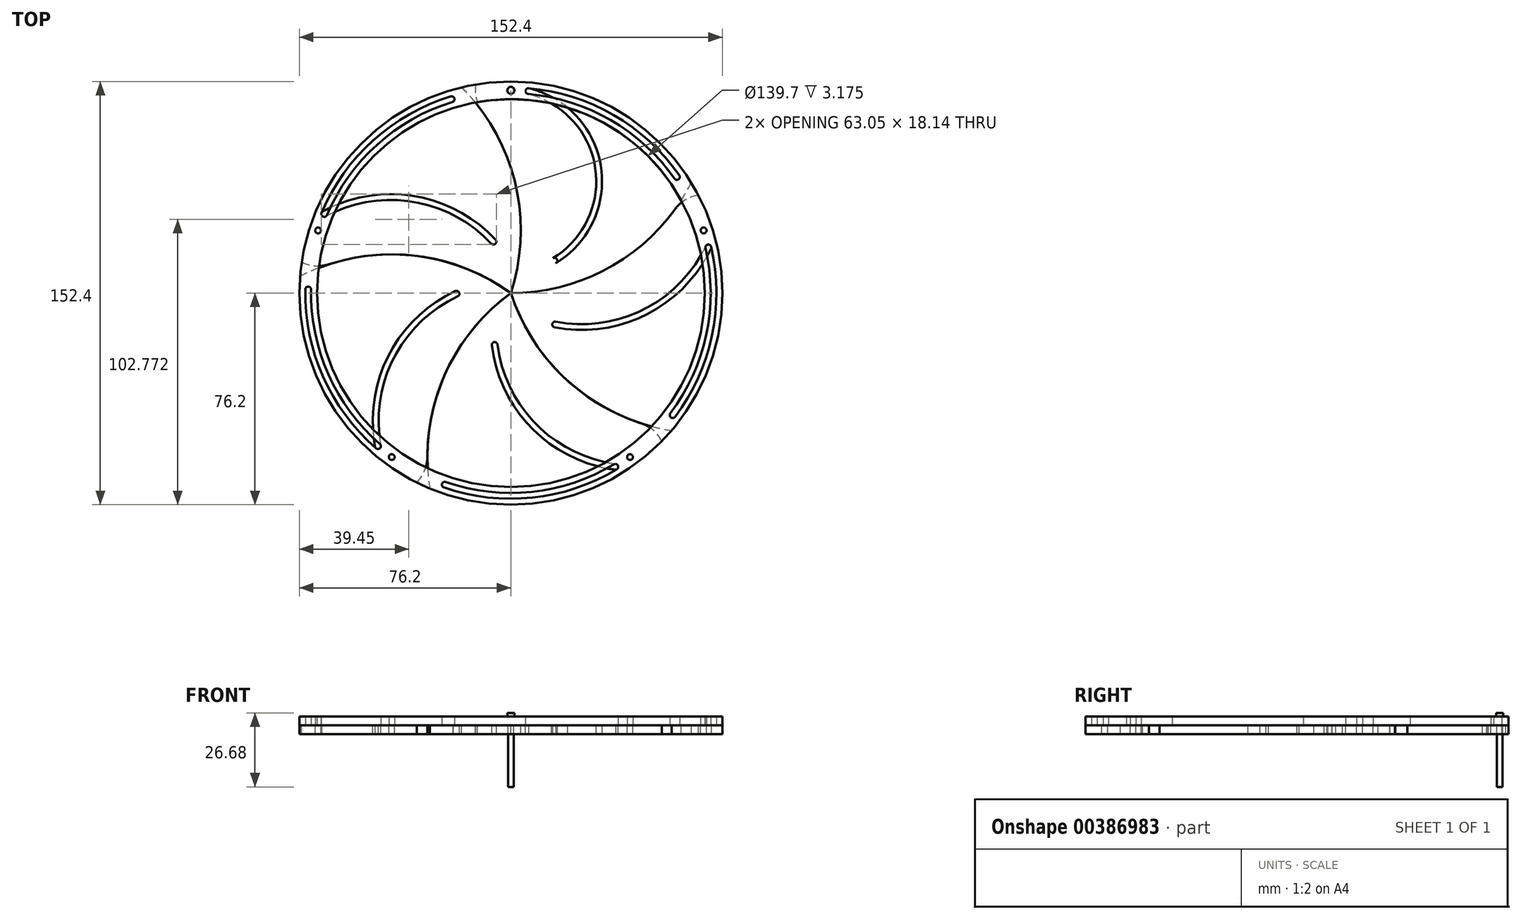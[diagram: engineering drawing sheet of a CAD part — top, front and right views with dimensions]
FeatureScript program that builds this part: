
annotation { "Feature Type Name" : "Feature", "Feature Type Description" : "" }
export const myFeature = defineFeature(function(context is Context, id is Id, definition is map)
    precondition{}
    {
        {
            var Q0;
            Q0=qCreatedBy(makeId("Top.planeOp"),FACE);
            var sketch = newSketch(context, id + "F0", { "sketchPlane" : qUnion([Q0])});
            skCircle(sketch, "E0", {"center": v(0, 0) * mm, "radius": 76.2 * mm});
            skCircle(sketch, "E1", {"center": v(0, 73.03) * mm, "radius": 1.05 * mm});
            skArc(sketch, "E2", {"start": v(0, 0) * mm, "mid": v(38.1, 10.73) * mm, "end": v(65, 39.76) * mm});
            skArc(sketch, "E3.1.0", {"start": v(0, 0) * mm, "mid": v(1.57, 39.55) * mm, "end": v(-17.72, 74.11) * mm});
            skCircle(sketch, "E3.1.1", {"center": v(-69.45, 22.57) * mm, "radius": 1.05 * mm});
            skArc(sketch, "E3.2.0", {"start": v(0, 0) * mm, "mid": v(-37.13, 13.72) * mm, "end": v(-75.96, 6.05) * mm});
            skCircle(sketch, "E3.2.1", {"center": v(-42.92, -59.08) * mm, "radius": 1.05 * mm});
            skArc(sketch, "E3.3.0", {"start": v(0, 0) * mm, "mid": v(-24.52, -31.07) * mm, "end": v(-29.22, -70.37) * mm});
            skCircle(sketch, "E3.3.1", {"center": v(42.92, -59.08) * mm, "radius": 1.05 * mm});
            skArc(sketch, "E3.4.0", {"start": v(0, 0) * mm, "mid": v(21.98, -32.92) * mm, "end": v(57.9, -49.54) * mm});
            skCircle(sketch, "E3.4.1", {"center": v(69.45, 22.57) * mm, "radius": 1.05 * mm});
            skArc(sketch, "E4", {"start": v(-12.64, 75.14) * mm, "mid": v(-12.48, 70.09) * mm, "end": v(-10.37, 65.49) * mm});
            skArc(sketch, "E5", {"start": v(6.44, 73.8) * mm, "mid": v(5.3, 72.84) * mm, "end": v(6.25, 71.7) * mm});
            skArc(sketch, "E6", {"start": v(58.97, 41.27) * mm, "mid": v(60.43, 41) * mm, "end": v(60.7, 42.47) * mm});
            skArc(sketch, "E7.trimOffspring", {"start": v(60.7, 42.47) * mm, "mid": v(37.04, 64.15) * mm, "end": v(6.44, 73.8) * mm});
            skArc(sketch, "E8.trimOffspring", {"start": v(58.97, 41.27) * mm, "mid": v(35.99, 62.33) * mm, "end": v(6.25, 71.7) * mm});
            skArc(sketch, "E9", {"start": v(14.79, 12.2) * mm, "mid": v(15.2, 10.78) * mm, "end": v(16.62, 11.2) * mm});
            skArc(sketch, "E10.1.0", {"start": v(-7.04, 17.84) * mm, "mid": v(-35.22, 32.9) * mm, "end": v(-66.73, 27.6) * mm});
            skArc(sketch, "E10.1.1", {"start": v(-5.5, 19.27) * mm, "mid": v(-35.07, 35) * mm, "end": v(-68.05, 29.26) * mm});
            skArc(sketch, "E10.1.2", {"start": v(-68.2, 28.92) * mm, "mid": v(-67.64, 27.55) * mm, "end": v(-66.26, 28.1) * mm});
            skArc(sketch, "E10.1.3", {"start": v(-21.64, 70.84) * mm, "mid": v(-49.57, 55.05) * mm, "end": v(-68.2, 28.92) * mm});
            skArc(sketch, "E10.1.4", {"start": v(-21.02, 68.84) * mm, "mid": v(-48.16, 53.49) * mm, "end": v(-66.26, 28.1) * mm});
            skArc(sketch, "E10.1.5", {"start": v(-21.02, 68.84) * mm, "mid": v(-20.33, 70.15) * mm, "end": v(-21.64, 70.84) * mm});
            skArc(sketch, "E10.1.6", {"start": v(-7.04, 17.84) * mm, "mid": v(-5.56, 17.78) * mm, "end": v(-5.5, 19.27) * mm});
            skArc(sketch, "E10.1.7", {"start": v(-75.37, 11.2) * mm, "mid": v(-70.51, 9.79) * mm, "end": v(-65.49, 10.37) * mm});
            skArc(sketch, "E10.2.0", {"start": v(-19.14, -1.19) * mm, "mid": v(-42.17, -23.33) * mm, "end": v(-46.86, -54.94) * mm});
            skArc(sketch, "E10.2.1", {"start": v(-20.03, 0.72) * mm, "mid": v(-44.12, -22.53) * mm, "end": v(-48.86, -55.68) * mm});
            skArc(sketch, "E10.2.2", {"start": v(-48.58, -55.92) * mm, "mid": v(-47.1, -55.81) * mm, "end": v(-47.2, -54.33) * mm});
            skArc(sketch, "E10.2.3", {"start": v(-74.06, 1.31) * mm, "mid": v(-67.67, -30.13) * mm, "end": v(-48.58, -55.92) * mm});
            skArc(sketch, "E10.2.4", {"start": v(-71.96, 1.28) * mm, "mid": v(-65.75, -29.27) * mm, "end": v(-47.2, -54.33) * mm});
            skArc(sketch, "E10.2.5", {"start": v(-71.96, 1.28) * mm, "mid": v(-73, 2.34) * mm, "end": v(-74.06, 1.31) * mm});
            skArc(sketch, "E10.2.6", {"start": v(-19.14, -1.19) * mm, "mid": v(-18.63, 0.2) * mm, "end": v(-20.03, 0.72) * mm});
            skArc(sketch, "E10.2.7", {"start": v(-33.94, -68.22) * mm, "mid": v(-31.1, -64.04) * mm, "end": v(-30.1, -59.08) * mm});
            skArc(sketch, "E10.3.0", {"start": v(-4.79, -18.57) * mm, "mid": v(9.16, -47.31) * mm, "end": v(37.77, -61.54) * mm});
            skArc(sketch, "E10.3.1", {"start": v(-6.87, -18.83) * mm, "mid": v(7.8, -48.92) * mm, "end": v(37.85, -63.67) * mm});
            skArc(sketch, "E10.3.2", {"start": v(38.17, -63.48) * mm, "mid": v(38.53, -62.04) * mm, "end": v(37.09, -61.68) * mm});
            skArc(sketch, "E10.3.3", {"start": v(-24.14, -70.03) * mm, "mid": v(7.74, -73.67) * mm, "end": v(38.17, -63.48) * mm});
            skArc(sketch, "E10.3.4", {"start": v(-23.45, -68.05) * mm, "mid": v(7.52, -71.58) * mm, "end": v(37.09, -61.68) * mm});
            skArc(sketch, "E10.3.5", {"start": v(-23.45, -68.05) * mm, "mid": v(-24.79, -68.7) * mm, "end": v(-24.14, -70.03) * mm});
            skArc(sketch, "E10.3.6", {"start": v(-4.79, -18.57) * mm, "mid": v(-5.96, -17.66) * mm, "end": v(-6.87, -18.83) * mm});
            skArc(sketch, "E10.3.7", {"start": v(54.4, -53.36) * mm, "mid": v(51.3, -49.37) * mm, "end": v(46.88, -46.88) * mm});
            skArc(sketch, "E10.4.0", {"start": v(16.18, -10.29) * mm, "mid": v(47.83, -5.9) * mm, "end": v(70.2, 16.9) * mm});
            skArc(sketch, "E10.4.1", {"start": v(15.78, -12.35) * mm, "mid": v(48.94, -7.7) * mm, "end": v(72.25, 16.33) * mm});
            skArc(sketch, "E10.4.2", {"start": v(72.17, 16.68) * mm, "mid": v(70.91, 17.47) * mm, "end": v(70.13, 16.21) * mm});
            skArc(sketch, "E10.4.3", {"start": v(59.15, -44.6) * mm, "mid": v(72.46, -15.4) * mm, "end": v(72.17, 16.68) * mm});
            skArc(sketch, "E10.4.4", {"start": v(57.47, -43.33) * mm, "mid": v(70.4, -14.96) * mm, "end": v(70.13, 16.21) * mm});
            skArc(sketch, "E10.4.5", {"start": v(57.47, -43.33) * mm, "mid": v(57.68, -44.8) * mm, "end": v(59.15, -44.6) * mm});
            skArc(sketch, "E10.4.6", {"start": v(16.18, -10.29) * mm, "mid": v(14.95, -11.12) * mm, "end": v(15.78, -12.35) * mm});
            skArc(sketch, "E10.4.7", {"start": v(67.56, 35.25) * mm, "mid": v(62.8, 33.53) * mm, "end": v(59.08, 30.1) * mm});
            skCircle(sketch, "E11", {"center": v(0, 0) * mm, "radius": 69.85 * mm});
            skCircle(sketch, "E12", {"center": v(15.7, 11.7) * mm, "radius": 1.05 * mm});
            skArc(sketch, "E13", {"start": v(6.6, 73.77) * mm, "mid": v(5.3, 72.92) * mm, "end": v(6.25, 71.7) * mm});
            skArc(sketch, "E14", {"start": v(15.7, 11.7) * mm, "mid": v(16.15, 11.98) * mm, "end": v(16.6, 12.26) * mm});
            skArc(sketch, "E15", {"start": v(15.16, 12.6) * mm, "mid": v(30.38, 45.2) * mm, "end": v(6.1, 71.73) * mm});
            skArc(sketch, "E16", {"start": v(16.25, 10.8) * mm, "mid": v(32.45, 45.55) * mm, "end": v(6.52, 73.79) * mm});
            skArc(sketch, "E17.trimOffspring", {"start": v(-20.72, 68.99) * mm, "mid": v(-20.75, 68.97) * mm, "end": v(-20.78, 68.95) * mm});
            skSolve(sketch);
        }
        {
            var Q0;
            Q0=qSketchRegion(id+"F0",true);
            var Q1;
            {var subQ1=sQuery(id+"F0.wireOp",EDGE,"E10.1.2");var subQ7=sQuery(id+"F0.wireOp",EDGE,"E10.1.0");var subQ8=makeQuery(id+"F0.imprint","INTERSECT",VERTEX,{"derivedFrom":[subQ7,subQ1]});Q1=makeQuery(id+"F0.imprint","IMPRINT",FACE,{"disambiguationData":[TD([[makeQuery(id+"F0.imprint","IMPRINT",EDGE,{"disambiguationData":[TD([[subQ8,1.0]])],"derivedFrom":subQ7}),-1.0]])]});}
            var Q2;
            {var subQ1=sQuery(id+"F0.wireOp",EDGE,"E5");var subQ6=sQuery(id+"F0.wireOp",EDGE,"E8.trimOffspring");var subQ9=makeQuery(id+"F0.imprint","INTERSECT",VERTEX,{"derivedFrom":[subQ1,subQ6]});Q2=makeQuery(id+"F0.imprint","IMPRINT",FACE,{"disambiguationData":[TD([[makeQuery(id+"F0.imprint","IMPRINT",EDGE,{"disambiguationData":[TD([[subQ9,1.0]])],"derivedFrom":subQ1}),-1.0]])]});}
            var Q3;
            {var subQ1=sQuery(id+"F0.wireOp",EDGE,"E10.4.2");var subQ7=sQuery(id+"F0.wireOp",EDGE,"E10.4.0");var subQ8=makeQuery(id+"F0.imprint","INTERSECT",VERTEX,{"derivedFrom":[subQ7,subQ1]});Q3=makeQuery(id+"F0.imprint","IMPRINT",FACE,{"disambiguationData":[TD([[makeQuery(id+"F0.imprint","IMPRINT",EDGE,{"disambiguationData":[TD([[subQ8,1.0]])],"derivedFrom":subQ7}),-1.0]])]});}
            var Q4;
            {var subQ1=sQuery(id+"F0.wireOp",EDGE,"E10.3.2");var subQ7=sQuery(id+"F0.wireOp",EDGE,"E10.3.0");var subQ8=makeQuery(id+"F0.imprint","INTERSECT",VERTEX,{"derivedFrom":[subQ7,subQ1]});Q4=makeQuery(id+"F0.imprint","IMPRINT",FACE,{"disambiguationData":[TD([[makeQuery(id+"F0.imprint","IMPRINT",EDGE,{"disambiguationData":[TD([[subQ8,1.0]])],"derivedFrom":subQ7}),-1.0]])]});}
            var Q5;
            {var subQ1=sQuery(id+"F0.wireOp",EDGE,"E10.2.2");var subQ7=sQuery(id+"F0.wireOp",EDGE,"E10.2.0");var subQ8=makeQuery(id+"F0.imprint","INTERSECT",VERTEX,{"derivedFrom":[subQ7,subQ1]});Q5=makeQuery(id+"F0.imprint","IMPRINT",FACE,{"disambiguationData":[TD([[makeQuery(id+"F0.imprint","IMPRINT",EDGE,{"disambiguationData":[TD([[subQ8,1.0]])],"derivedFrom":subQ7}),-1.0]])]});}
            var Q6;
            {var subQ1=sQuery(id+"F0.wireOp",EDGE,"E13");var subQ7=sQuery(id+"F0.wireOp",EDGE,"E8.trimOffspring");var subQ8=makeQuery(id+"F0.imprint","INTERSECT",VERTEX,{"derivedFrom":[subQ7,subQ1]});Q6=makeQuery(id+"F0.imprint","IMPRINT",FACE,{"disambiguationData":[TD([[makeQuery(id+"F0.imprint","IMPRINT",EDGE,{"disambiguationData":[TD([[subQ8,1.0]])],"derivedFrom":subQ7}),1.0]])]});}
            extrude(context, id + "F1", {"entities" : qUnion([Q0, Q1, Q2, Q3, Q4, Q5, Q6]), "depth" : 3.17 * mm});
        }
        {
            var Q0;
            {var subQ10=sQuery(id+"F0.wireOp",EDGE,"E9");Q0=makeQuery(id+"F0.imprint","IMPRINT",FACE,{"disambiguationData":[TD([[makeQuery(id+"F0.imprint","IMPRINT",EDGE,{"derivedFrom":subQ10}),-1.0]])]});}
            var Q1;
            Q1=makeQuery(id+"F0.imprint","IMPRINT",FACE,{"disambiguationData":[TD([[makeQuery(id+"F0.imprint","IMPRINT",EDGE,{"derivedFrom":sQuery(id+"F0.wireOp",EDGE,"E1")}),-1.0]])]});
            var Q2;
            {var subQ0=sQuery(id+"F0.wireOp",EDGE,"E6");Q2=makeQuery(id+"F0.imprint","IMPRINT",FACE,{"disambiguationData":[TD([[makeQuery(id+"F0.imprint","IMPRINT",EDGE,{"derivedFrom":subQ0}),1.0]])]});}
            var Q3;
            {var subQ11=sQuery(id+"F0.wireOp",EDGE,"E12");var subQ13=makeQuery(id+"F0.imprint","IMPRINT",VERTEX,{"disambiguationData":[OD(1.0)],"derivedFrom":subQ11});Q3=makeQuery(id+"F0.imprint","IMPRINT",FACE,{"disambiguationData":[TD([[makeQuery(id+"F0.imprint","IMPRINT",EDGE,{"disambiguationData":[TD([[subQ13,1.0]])],"derivedFrom":subQ11}),-1.0]])]});}
            extrude(context, id + "F2", {"entities" : qUnion([Q0, Q1, Q2, Q3]), "depth" : -3.17 * mm});
        }
        {
            var Q0;
            {var subQ0=sQuery(id+"F0.wireOp",EDGE,"E10.4.6");Q0=makeQuery(id+"F0.imprint","IMPRINT",FACE,{"disambiguationData":[TD([[makeQuery(id+"F0.imprint","IMPRINT",EDGE,{"derivedFrom":subQ0}),-1.0]])]});}
            var Q1;
            Q1=makeQuery(id+"F0.imprint","IMPRINT",FACE,{"disambiguationData":[TD([[makeQuery(id+"F0.imprint","IMPRINT",EDGE,{"derivedFrom":sQuery(id+"F0.wireOp",EDGE,"E3.4.1")}),-1.0]])]});
            var Q2;
            {var subQ5=sQuery(id+"F0.wireOp",EDGE,"E10.4.5");Q2=makeQuery(id+"F0.imprint","IMPRINT",FACE,{"disambiguationData":[TD([[makeQuery(id+"F0.imprint","IMPRINT",EDGE,{"derivedFrom":subQ5}),1.0]])]});}
            extrude(context, id + "F3", {"entities" : qUnion([Q0, Q1, Q2]), "oppositeDirection" : true, "depth" : 3.17 * mm});
        }
        {
            var Q0;
            {var subQ5=sQuery(id+"F0.wireOp",EDGE,"E10.1.5");Q0=makeQuery(id+"F0.imprint","IMPRINT",FACE,{"disambiguationData":[TD([[makeQuery(id+"F0.imprint","IMPRINT",EDGE,{"derivedFrom":subQ5}),1.0]])]});}
            var Q1;
            Q1=makeQuery(id+"F0.imprint","IMPRINT",FACE,{"disambiguationData":[TD([[makeQuery(id+"F0.imprint","IMPRINT",EDGE,{"derivedFrom":sQuery(id+"F0.wireOp",EDGE,"E3.1.1")}),-1.0]])]});
            var Q2;
            {var subQ5=sQuery(id+"F0.wireOp",EDGE,"E10.1.6");Q2=makeQuery(id+"F0.imprint","IMPRINT",FACE,{"disambiguationData":[TD([[makeQuery(id+"F0.imprint","IMPRINT",EDGE,{"derivedFrom":subQ5}),-1.0]])]});}
            extrude(context, id + "F4", {"entities" : qUnion([Q0, Q1, Q2]), "oppositeDirection" : true, "depth" : 3.17 * mm});
        }
        {
            var Q0;
            {var subQ5=sQuery(id+"F0.wireOp",EDGE,"E10.2.5");Q0=makeQuery(id+"F0.imprint","IMPRINT",FACE,{"disambiguationData":[TD([[makeQuery(id+"F0.imprint","IMPRINT",EDGE,{"derivedFrom":subQ5}),1.0]])]});}
            var Q1;
            Q1=makeQuery(id+"F0.imprint","IMPRINT",FACE,{"disambiguationData":[TD([[makeQuery(id+"F0.imprint","IMPRINT",EDGE,{"derivedFrom":sQuery(id+"F0.wireOp",EDGE,"E3.2.1")}),-1.0]])]});
            var Q2;
            {var subQ0=sQuery(id+"F0.wireOp",EDGE,"E10.2.6");Q2=makeQuery(id+"F0.imprint","IMPRINT",FACE,{"disambiguationData":[TD([[makeQuery(id+"F0.imprint","IMPRINT",EDGE,{"derivedFrom":subQ0}),-1.0]])]});}
            extrude(context, id + "F5", {"entities" : qUnion([Q0, Q1, Q2]), "oppositeDirection" : true, "depth" : 3.17 * mm});
        }
        {
            var Q0;
            {var subQ5=sQuery(id+"F0.wireOp",EDGE,"E10.3.5");Q0=makeQuery(id+"F0.imprint","IMPRINT",FACE,{"disambiguationData":[TD([[makeQuery(id+"F0.imprint","IMPRINT",EDGE,{"derivedFrom":subQ5}),1.0]])]});}
            var Q1;
            Q1=makeQuery(id+"F0.imprint","IMPRINT",FACE,{"disambiguationData":[TD([[makeQuery(id+"F0.imprint","IMPRINT",EDGE,{"derivedFrom":sQuery(id+"F0.wireOp",EDGE,"E3.3.1")}),-1.0]])]});
            var Q2;
            {var subQ0=sQuery(id+"F0.wireOp",EDGE,"E10.3.6");Q2=makeQuery(id+"F0.imprint","IMPRINT",FACE,{"disambiguationData":[TD([[makeQuery(id+"F0.imprint","IMPRINT",EDGE,{"derivedFrom":subQ0}),-1.0]])]});}
            extrude(context, id + "F6", {"entities" : qUnion([Q0, Q1, Q2]), "oppositeDirection" : true, "depth" : 3.17 * mm});
        }
        {
            var Q0;
            Q0=makeQuery(id+"F1.opExtrude","CAP_FACE",FACE,{"disambiguationData":[OSD([sQuery(id+"F0.wireOp",EDGE,"E0"),sQuery(id+"F0.wireOp",EDGE,"E1"),sQuery(id+"F0.wireOp",EDGE,"E3.1.1"),sQuery(id+"F0.wireOp",EDGE,"E3.2.1"),sQuery(id+"F0.wireOp",EDGE,"E3.3.1"),sQuery(id+"F0.wireOp",EDGE,"E3.4.1"),sQuery(id+"F0.wireOp",EDGE,"E5"),sQuery(id+"F0.wireOp",EDGE,"E6"),sQuery(id+"F0.wireOp",EDGE,"E7.trimOffspring"),sQuery(id+"F0.wireOp",EDGE,"E8.trimOffspring"),sQuery(id+"F0.wireOp",EDGE,"E10.1.2"),sQuery(id+"F0.wireOp",EDGE,"E10.1.3"),sQuery(id+"F0.wireOp",EDGE,"E10.1.4"),sQuery(id+"F0.wireOp",EDGE,"E10.1.5"),sQuery(id+"F0.wireOp",EDGE,"E10.2.2"),sQuery(id+"F0.wireOp",EDGE,"E10.2.3"),sQuery(id+"F0.wireOp",EDGE,"E10.2.4"),sQuery(id+"F0.wireOp",EDGE,"E10.2.5"),sQuery(id+"F0.wireOp",EDGE,"E10.3.2"),sQuery(id+"F0.wireOp",EDGE,"E10.3.3"),sQuery(id+"F0.wireOp",EDGE,"E10.3.4"),sQuery(id+"F0.wireOp",EDGE,"E10.3.5"),sQuery(id+"F0.wireOp",EDGE,"E10.4.2"),sQuery(id+"F0.wireOp",EDGE,"E10.4.3"),sQuery(id+"F0.wireOp",EDGE,"E10.4.4"),sQuery(id+"F0.wireOp",EDGE,"E10.4.5"),sQuery(id+"F0.wireOp",EDGE,"E11")])],"isStart":false});
            var sketch = newSketch(context, id + "F7", { "sketchPlane" : qUnion([Q0])});
            skCircle(sketch, "E18", {"center": v(0, 73.03) * mm, "radius": 1.05 * mm});
            skCircle(sketch, "E19", {"center": v(0, 73.03) * mm, "radius": 1.27 * mm});
            skSolve(sketch);
        }
        {
            var Q0;
            Q0=makeQuery(id+"F7.imprint","IMPRINT",FACE,{"disambiguationData":[TD([[makeQuery(id+"F7.imprint","IMPRINT",EDGE,{"derivedFrom":sQuery(id+"F7.wireOp",EDGE,"E18")}),1.0]])]});
            extrude(context, id + "F8", {"entities" : qUnion([Q0]), "oppositeDirection" : true, "depth" : 25.4 * mm});
        }
        {
            var Q0;
            Q0=makeQuery(id+"F7.imprint","IMPRINT",FACE,{"disambiguationData":[TD([[makeQuery(id+"F7.imprint","IMPRINT",EDGE,{"derivedFrom":sQuery(id+"F7.wireOp",EDGE,"E18")}),1.0]])]});
            var Q1;
            Q1=makeQuery(id+"F7.imprint","IMPRINT",FACE,{"disambiguationData":[TD([[makeQuery(id+"F7.imprint","IMPRINT",EDGE,{"derivedFrom":sQuery(id+"F7.wireOp",EDGE,"E18")}),-1.0]])]});
            extrude(context, id + "F9", {"entities" : qUnion([Q0, Q1]), "operationType" : NewBodyOperationType.ADD, "depth" : 1.27 * mm});
        }
    });
